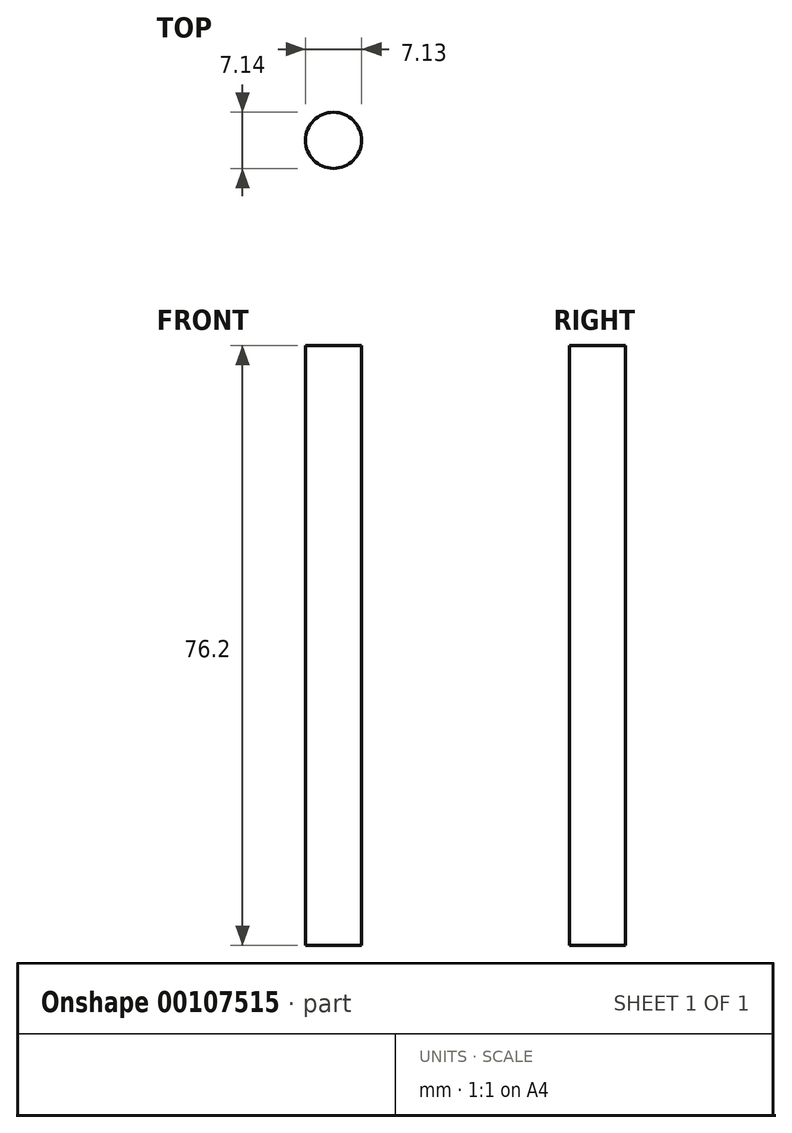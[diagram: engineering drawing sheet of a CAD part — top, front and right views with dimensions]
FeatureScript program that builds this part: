
annotation { "Feature Type Name" : "Feature", "Feature Type Description" : "" }
export const myFeature = defineFeature(function(context is Context, id is Id, definition is map)
    precondition{}
    {
        {
            var Q0;
            Q0=qCreatedBy(makeId("Front.planeOp"),FACE);
            var sketch = newSketch(context, id + "F0", { "sketchPlane" : qUnion([Q0])});
            skLineSegment(sketch, "E0", {"start": v(-55.43, 38.95) * mm, "end": v(-55.43, -37.25) * mm});
            skLineSegment(sketch, "E1", {"start": v(-55.43, -37.25) * mm, "end": v(39.82, -37.25) * mm});
            skLineSegment(sketch, "E2", {"start": v(39.82, -37.25) * mm, "end": v(39.82, 38.95) * mm});
            skLineSegment(sketch, "E3", {"start": v(39.82, 38.95) * mm, "end": v(-55.43, 38.95) * mm});
            skLineSegment(sketch, "E4", {"start": v(-55.43, 0.85) * mm, "end": v(39.82, 0.85) * mm, "construction": true});
            skLineSegment(sketch, "E5", {"start": v(-7.8, 38.95) * mm, "end": v(-7.8, -37.25) * mm, "construction": true});
            skCircle(sketch, "E6", {"center": v(-7.8, 0.85) * mm, "radius": 23.75 * mm});
            skSolve(sketch);
        }
        {
            var Q0;
            Q0=makeQuery(id+"F0.imprint","IMPRINT",FACE,{"disambiguationData":[TD([[makeQuery(id+"F0.imprint","IMPRINT",EDGE,{"derivedFrom":sQuery(id+"F0.wireOp",EDGE,"E0")}),1.0]])]});
            extrude(context, id + "F1", {"entities" : qUnion([Q0]), "endBound" : BoundingType.SYMMETRIC, "depth" : 25.4 * mm});
        }
        {
            var Q0;
            Q0=makeQuery(id+"F1.opExtrude","SWEPT_FACE",FACE,{"disambiguationData":[OSD([sQuery(id+"F0.wireOp",EDGE,"E3")])]});
            var sketch = newSketch(context, id + "F2", { "sketchPlane" : qUnion([Q0])});
            skLineSegment(sketch, "E7", {"start": v(-55.43, 0) * mm, "end": v(-45.9, 0) * mm, "construction": true});
            skPoint(sketch, "E7.endSnap0", {"position": v(-55.43, 0) * mm});
            skCircle(sketch, "E8", {"center": v(-45.9, 0) * mm, "radius": 3.57 * mm});
            skLineSegment(sketch, "E9", {"start": v(-7.8, 12.7) * mm, "end": v(-7.8, -12.7) * mm, "construction": true});
            skCircle(sketch, "E10.MirrorC", {"center": v(30.3, 0) * mm, "radius": 3.57 * mm});
            skSolve(sketch);
        }
        {
            var Q0;
            Q0=makeQuery(id+"F2.imprint","IMPRINT",FACE,{"disambiguationData":[TD([[makeQuery(id+"F2.imprint","IMPRINT",EDGE,{"derivedFrom":sQuery(id+"F2.wireOp",EDGE,"E8")}),1.0]])]});
            var Q1;
            Q1=makeQuery(id+"F2.imprint","IMPRINT",FACE,{"disambiguationData":[TD([[makeQuery(id+"F2.imprint","IMPRINT",EDGE,{"derivedFrom":sQuery(id+"F2.wireOp",EDGE,"E10.MirrorC")}),-1.0]])]});
            extrude(context, id + "F3", {"entities" : qUnion([Q0, Q1]), "operationType" : NewBodyOperationType.REMOVE, "oppositeDirection" : true, "depth" : 76.2 * mm});
        }
    });
